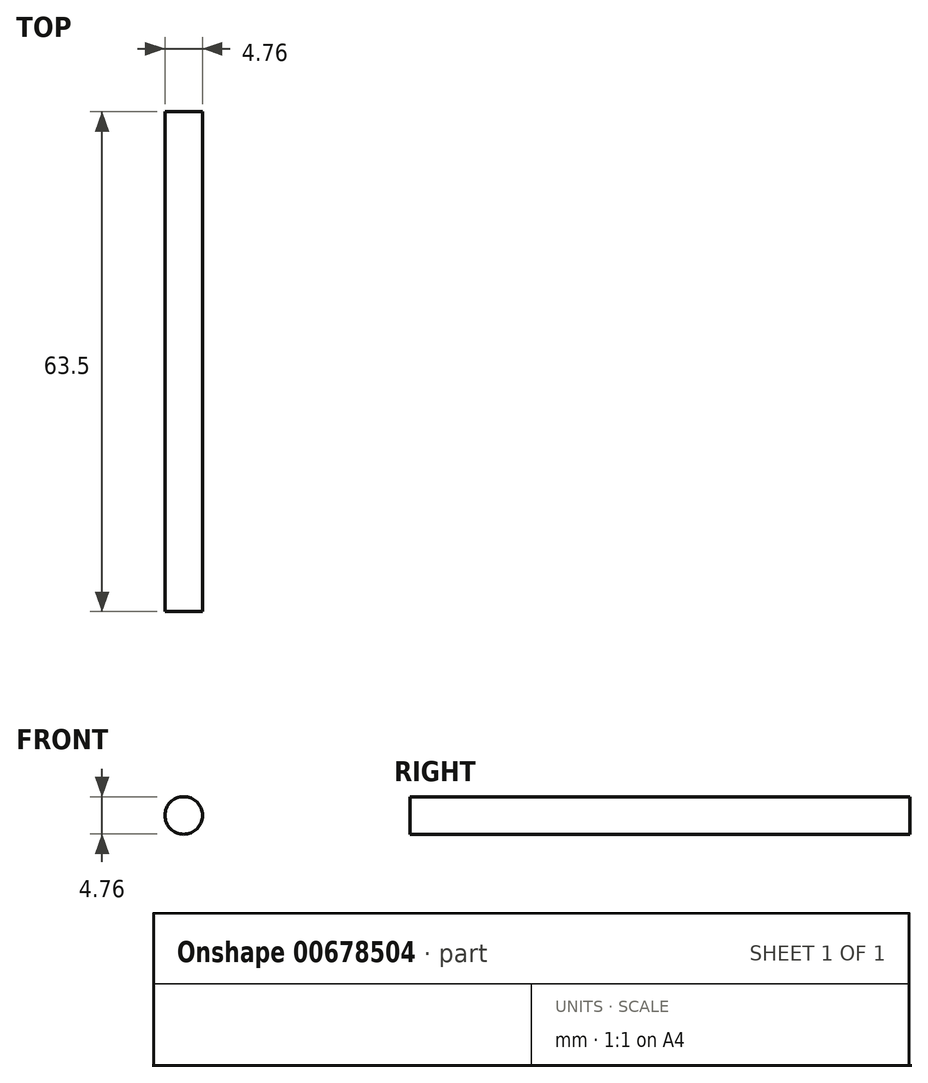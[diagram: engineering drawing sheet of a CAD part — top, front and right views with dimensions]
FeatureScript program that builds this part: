
annotation { "Feature Type Name" : "Feature", "Feature Type Description" : "" }
export const myFeature = defineFeature(function(context is Context, id is Id, definition is map)
    precondition{}
    {
        {
            var Q0;
            Q0=qCreatedBy(makeId("Front.planeOp"),FACE);
            var sketch = newSketch(context, id + "F0", { "sketchPlane" : qUnion([Q0])});
            skCircle(sketch, "E0", {"center": v(0, 0) * mm, "radius": 2.38 * mm});
            skSolve(sketch);
        }
        {
            var Q0;
            Q0=sQuery(id+"F0.wireOp",EDGE,"E0");
            extrude(context, id + "F1", {"bodyType" : ToolBodyType.SURFACE, "surfaceEntities" : qUnion([Q0]), "depth" : 63.5 * mm, "offsetDistance" : 25.4 * mm});
        }
    });
